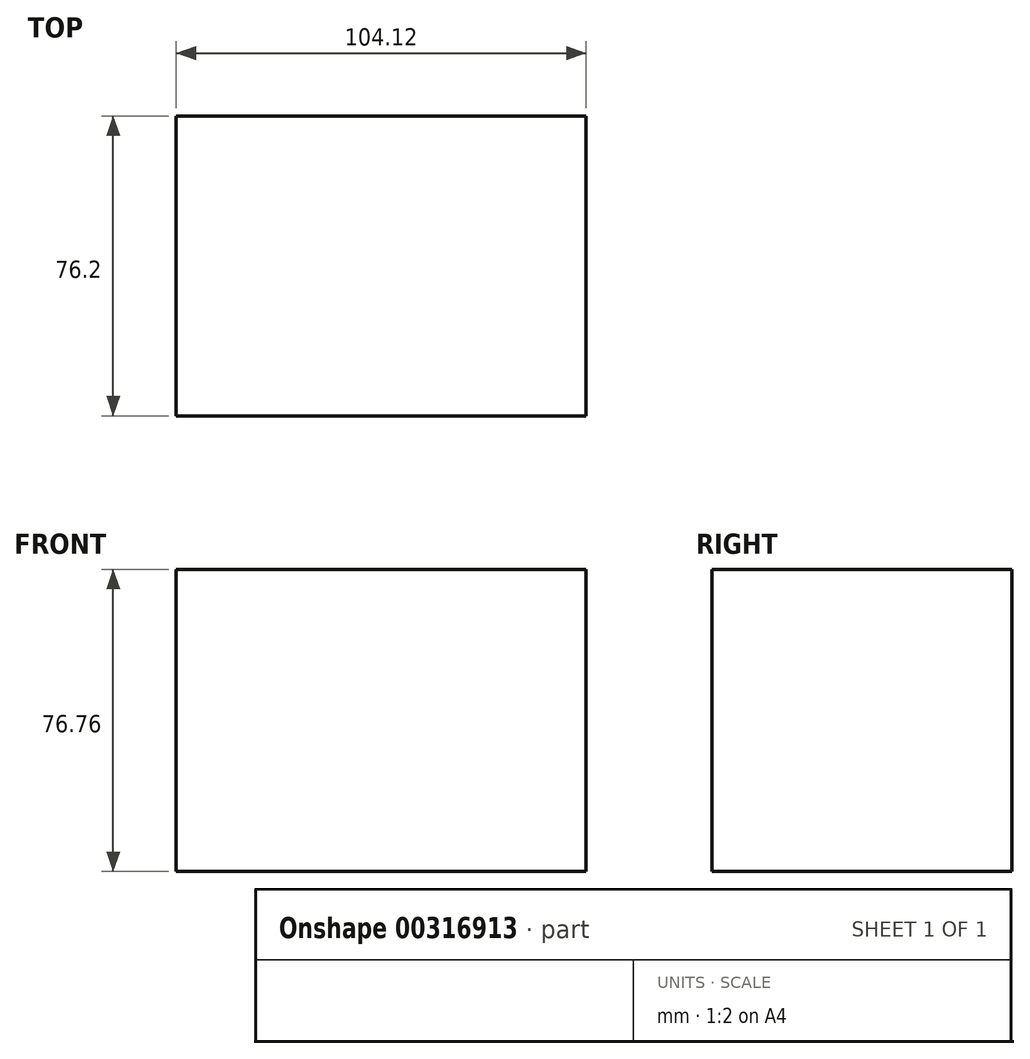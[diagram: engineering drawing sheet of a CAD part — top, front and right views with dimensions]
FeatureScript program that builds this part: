
annotation { "Feature Type Name" : "Feature", "Feature Type Description" : "" }
export const myFeature = defineFeature(function(context is Context, id is Id, definition is map)
    precondition{}
    {
        {
            var Q0;
            Q0=qCreatedBy(makeId("Front.planeOp"),FACE);
            var sketch = newSketch(context, id + "F0", { "sketchPlane" : qUnion([Q0])});
            skLineSegment(sketch, "E0.bottom", {"start": v(-39.26, 0) * mm, "end": v(64.86, 0) * mm});
            skLineSegment(sketch, "E0.top", {"start": v(-39.26, 76.76) * mm, "end": v(64.86, 76.76) * mm});
            skLineSegment(sketch, "E0.left", {"start": v(-39.26, 0) * mm, "end": v(-39.26, 76.76) * mm});
            skLineSegment(sketch, "E0.right", {"start": v(64.86, 0) * mm, "end": v(64.86, 76.76) * mm});
            skSolve(sketch);
        }
        {
            var Q0;
            Q0 = qSketchRegion(id + "F0", true);
            extrude(context, id + "F1", {"entities" : qUnion([Q0]), "depth" : 76.2 * mm});
        }
    });
